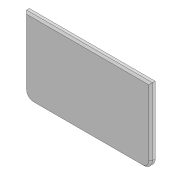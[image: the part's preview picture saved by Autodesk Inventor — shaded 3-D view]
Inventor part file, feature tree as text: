
AUTODESK INVENTOR PART (.ipt)
format: ipt  version: 2020 (Build 240168000, 168)  size: 90,112 bytes
history: native  units: mm
features: extrude x1, chamfer x1, sketch x1
ambient origin geometry x8: Origin, YZ Plane, XZ Plane, XY Plane, X Axis, Y Axis, Z Axis, Center Point
bodies: Solid1 (feature_tree)
feature tree (3):
  extrude  "Extrusion1"  Depth=168.0mm
  chamfer  "Chamfer1"  Distance=19.0mm
  sketch  "Sketch1"  dims[d0=278.0mm d1=168.0mm d2=19.0mm d3=10.0mm d4=0.0mm d5=4.0mm d6=2.0mm d7=45.0deg]
